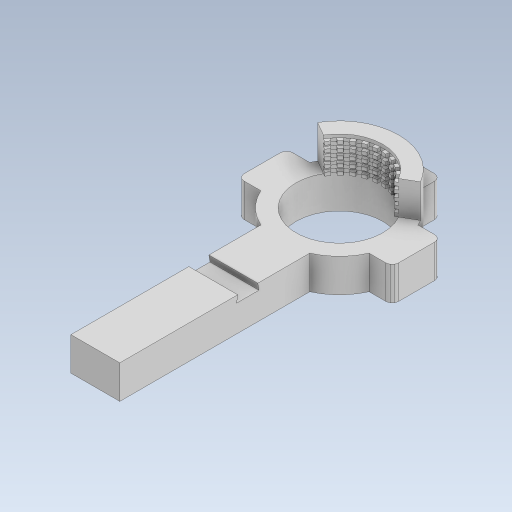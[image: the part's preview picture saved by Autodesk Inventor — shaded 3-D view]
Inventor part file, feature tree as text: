
AUTODESK INVENTOR PART (.ipt)
format: ipt  version: 2023 (Build 270158000, 158)  size: 438,272 bytes
history: native  units: in
note: dims shown in document units (in); Inventor stores cm internally (conversion verified against a paired STEP export)
features: sketch x6, extrude x5, revolve x1
ambient origin geometry x8: Origin, YZ Plane, XZ Plane, XY Plane, X Axis, Y Axis, Z Axis, Center Point
bodies: Solid1 (feature_tree)
feature tree (12):
  extrude  "Extrusion1"  Depth=0.3937in TaperAngle=0.0deg
  extrude  "Extrusion2"  Depth=0.3937in TaperAngle=0.0deg
  extrude  "Extrusion3"  Depth=0.0394in TaperAngle=120.0deg
  revolve  "Revolution1"  [1 undecoded]
  extrude  "Extrusion4"  Depth=0.1969in TaperAngle=0.0deg
  extrude  "Extrusion5"  Depth=0.0787in
  sketch  "Sketch1"  dims[d0=1.0236in d1=0.3937in d2=0.0in]
  sketch  "Sketch2"  dims[d3=120.0deg d4=0.3937in d5=0.0in]
  sketch  "Sketch3"  dims[d6=0.0394in d7=7.874in d9=120.0deg]
  sketch  "Sketch4"  dims[d11=0.3937in d12=0.0in d14=3.937in d16=0.0394in d17=0.3937in d19=0.3937in]
  sketch  "Sketch5"  dims[d21=360.0deg d22=1.9685in d23=0.1969in d24=0.0in d25=0.0in]
  sketch  "Sketch6"  dims[d26=0.2362in d27=1.2511in d28=1.3998in d29=0.0787in d30=0.0687in]
note: 1 required parameter value undecoded (feature->parameter linkage not recoverable at this tier; creation-order binding heuristic only, values carry confidence <= 0.55)
